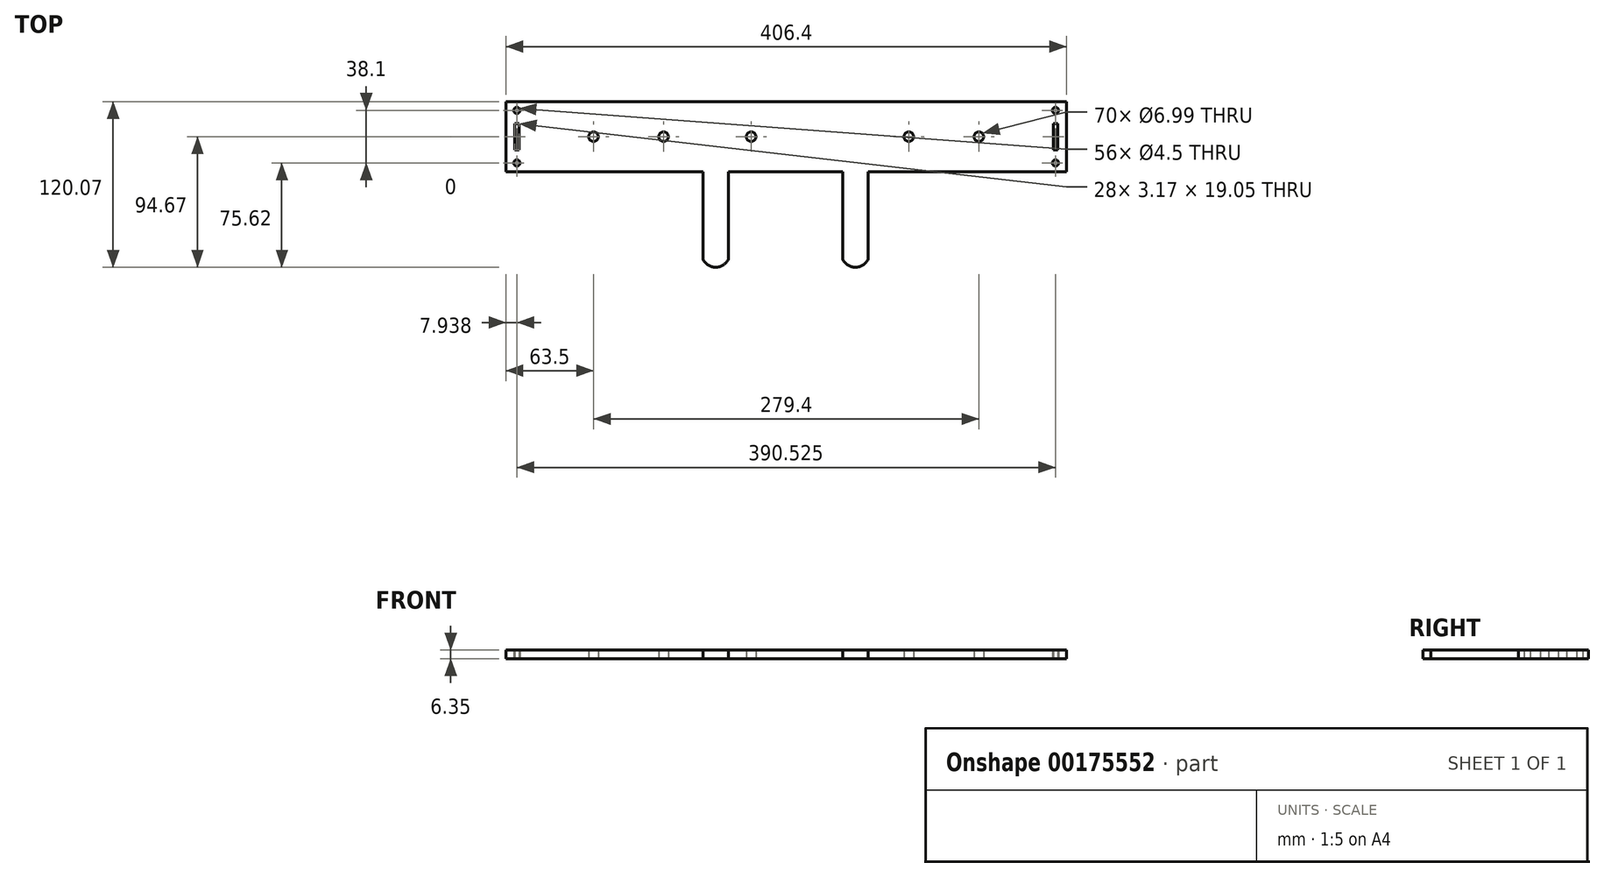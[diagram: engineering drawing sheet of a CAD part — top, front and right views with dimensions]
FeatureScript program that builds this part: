
annotation { "Feature Type Name" : "Feature", "Feature Type Description" : "" }
export const myFeature = defineFeature(function(context is Context, id is Id, definition is map)
    precondition{}
    {
        {
            var Q0;
            Q0=qCreatedBy(makeId("Top.planeOp"),FACE);
            var sketch = newSketch(context, id + "F0", { "sketchPlane" : qUnion([Q0])});
            skLineSegment(sketch, "E0.bottom", {"start": v(203.2, 25.4) * mm, "end": v(-203.2, 25.4) * mm});
            skLineSegment(sketch, "E0.top", {"start": v(203.2, -25.4) * mm, "end": v(-203.2, -25.4) * mm});
            skLineSegment(sketch, "E0.left", {"start": v(203.2, 25.4) * mm, "end": v(203.2, -25.4) * mm});
            skLineSegment(sketch, "E0.right", {"start": v(-203.2, 25.4) * mm, "end": v(-203.2, -25.4) * mm});
            skCircle(sketch, "E1", {"center": v(-139.7, 0) * mm, "radius": 3.5 * mm});
            skCircle(sketch, "E2", {"center": v(-88.9, 0) * mm, "radius": 3.5 * mm});
            skLineSegment(sketch, "E3", {"start": v(0, 25.4) * mm, "end": v(0, -25.4) * mm, "construction": true});
            skCircle(sketch, "E4.MirrorC", {"center": v(139.7, 0) * mm, "radius": 3.5 * mm});
            skCircle(sketch, "E5.MirrorC", {"center": v(88.9, 0) * mm, "radius": 3.5 * mm});
            skLineSegment(sketch, "E6.bottom", {"start": v(196.85, -9.52) * mm, "end": v(193.67, -9.52) * mm});
            skLineSegment(sketch, "E6.top", {"start": v(196.85, 9.53) * mm, "end": v(193.67, 9.53) * mm});
            skLineSegment(sketch, "E6.left", {"start": v(196.85, -9.53) * mm, "end": v(196.85, 9.52) * mm});
            skLineSegment(sketch, "E6.right", {"start": v(193.68, -9.53) * mm, "end": v(193.68, 9.52) * mm});
            skPoint(sketch, "E6.middle", {"position": v(195.26, 0) * mm});
            skCircle(sketch, "E7", {"center": v(195.26, 19.05) * mm, "radius": 2.25 * mm});
            skPoint(sketch, "E7.centerSnap0", {"position": v(195.26, 9.53) * mm});
            skCircle(sketch, "E8.MirrorC", {"center": v(195.26, -19.05) * mm, "radius": 2.25 * mm});
            skCircle(sketch, "E9.MirrorC", {"center": v(-195.26, 19.05) * mm, "radius": 2.25 * mm});
            skLineSegment(sketch, "E10.MirrorCS", {"start": v(-193.68, -9.53) * mm, "end": v(-193.68, 9.52) * mm});
            skCircle(sketch, "E11.MirrorC", {"center": v(-195.26, -19.05) * mm, "radius": 2.25 * mm});
            skPoint(sketch, "E12.MirrorP", {"position": v(-195.26, 9.53) * mm});
            skLineSegment(sketch, "E13.MirrorCS", {"start": v(-196.85, 9.53) * mm, "end": v(-193.67, 9.53) * mm});
            skLineSegment(sketch, "E14.MirrorCS", {"start": v(-196.85, -9.53) * mm, "end": v(-193.67, -9.53) * mm});
            skLineSegment(sketch, "E15.MirrorCS", {"start": v(-196.85, -9.53) * mm, "end": v(-196.85, 9.52) * mm});
            skLineSegment(sketch, "E16.left", {"start": v(-60.33, -25.4) * mm, "end": v(-60.33, -88.9) * mm});
            skLineSegment(sketch, "E16.right", {"start": v(-42, -25.4) * mm, "end": v(-42, -88.9) * mm});
            skLineSegment(sketch, "E17.MirrorCS", {"start": v(40.98, -25.4) * mm, "end": v(40.98, -88.9) * mm});
            skLineSegment(sketch, "E18.MirrorCS", {"start": v(59.3, -25.4) * mm, "end": v(59.3, -88.9) * mm});
            skArc(sketch, "E19", {"start": v(-60.33, -88.9) * mm, "mid": v(-51.17, -94.67) * mm, "end": v(-42, -88.9) * mm});
            skArc(sketch, "E20", {"start": v(40.98, -88.9) * mm, "mid": v(50.15, -94.67) * mm, "end": v(59.3, -88.9) * mm});
            skCircle(sketch, "E21", {"center": v(-25.4, 0) * mm, "radius": 3.5 * mm});
            skSolve(sketch);
        }
        {
            var Q0;
            Q0 = qSketchRegion(id + "F0", true);
            extrude(context, id + "F1", {"entities" : qUnion([Q0]), "depth" : 6.35 * mm});
        }
    });
